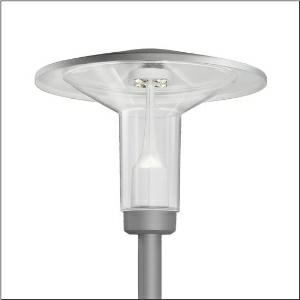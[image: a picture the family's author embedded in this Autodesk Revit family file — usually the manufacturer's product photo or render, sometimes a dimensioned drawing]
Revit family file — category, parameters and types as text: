
# Revit family: laterne_iq___pl1_2s_5xa5255cf14h_64ad
name_source: partatom
category: Lighting Fixtures
units: mm (PartAtom-declared; Revit-internal decimal feet)

## family parameters
Cut with Voids When Loaded = No
Host = Face
Light Source = No
Part Type = Normal
Room Calculation Point = No
Round Connector Dimension = Use Diameter
Shared = No

## types (1)
- --- (1 x LED, 2970 lm, 23.9 W, 2200K)
    Apparent Load = 24 VA
    CIE Flux Codes = 25 63 94 98 100
    Color Rendering = 70
    Color Temperature = 2200K
    Default Elevation = 1800 mm
    Description = Lantern iQ, mast luminaire, Module 540 iQ-SR, primary light control with 3 zone facetted reflector, of plastic, silver coated, highly specular, structured, primary optical cover: cover, of PMMA, transparent, light distribution: PL1.2s, light emission: direct distribution, primary light characteristic: symmetric, installation type: post-top, LED, High Power LED, rated luminous flux: 2.970lm, luminous efficacy: 124lm/W, light colour: 722, colour temperature: 2200K, control gear: iQ Street-Remote, control: pre-setting: logarithmic dimming characteristic, Street-Remote, Auto-Match, Temp-Guard, Lumen-Switch, Night-Set, Smart-Wire, Light-Fading, Desk-Remote (wireless, voltage-free reading and setting of iQ features in the workshop via application-optimized NFC function/RFID function), optimised constant luminous flux control (CLO 2.0), with terminal, 6-pole, max. 2.5mm², mains connection: 230..240V, AC, 50/60Hz, start of lifetime: 24W, end of service life: 26W, reduction: 12W, luminaire housing, upper part, of glass-fibre reinforced polyester, coated, Siteco® metallic grey (DB 702S), diameter: 750mm, height: 583mm, spigot size: d x l = 76 x 70mm (post-top) | with reducer (optional accessory) 60 x 70mm, mounting height: 3..5m, post-top mast mounting element, of diecast aluminium, coated, Siteco® metallic grey (DB 702S), Module 540 iQ-SR, traffic white (RAL 9016), equipment: standard, protection rating (complete): IP65, insulation class (complete): insulation class II (safety insulation), certification: CE, ENEC, VDE, packaging unit: 1 piece

Light Distribution: PL1.2s
    Height = 583 mm
    Lamp = 1 x LED
    Lamp Light Flux = 2970 lm
    Lamp Power = 23.9 W
    Lamp count = 1
    Length = 750 mm
    Luminous efficacy = 124 lm/W
    Manufacturer = Siteco
    ModVariant = No
    Model = 5XA5255CF14H
    Number of Poles = 1
    OnlyDefault = Yes
    Power Factor = 1
    Product Name = Laterne iQ | PL1.2s
    Product group = mast luminaire | pylon top
    ProductGroupID = 6100
    Protection Class = Protection class II
    Protection Degree = IP 65
    RLX_Detail_Level = 1
    RLX_Emergency_Light_Flux = 0 lm
    RLX_Emergency_Type = 0
    RLX_Emergency_Type_DB = No
    RlxData = <blob elided: 31765 chars, md5=490f6611>
    Socket = socket
    Standby Power = 0 W
    System Light Flux = 2970 lm
    System Power = 24 W
    Type Comments = factory setting: luminous flux: 100 % | dim-lin: 254 | 499 mA
    Type Image = l_1006050.jpg
    URL = http://relux.com
    VarID = @adj_167437
    Voltage = 0 V
    Weight = 0.00 kg
    Width = 0 mm  [stored 0 ft]

note: [stored X ft] marks values corroborated as IEEE doubles in the binary element streams (Revit-internal decimal feet)

## geometry (parser evidence)
native form markers: Blend x4, Sweep x8
no freeform markers — native parametric forms only
